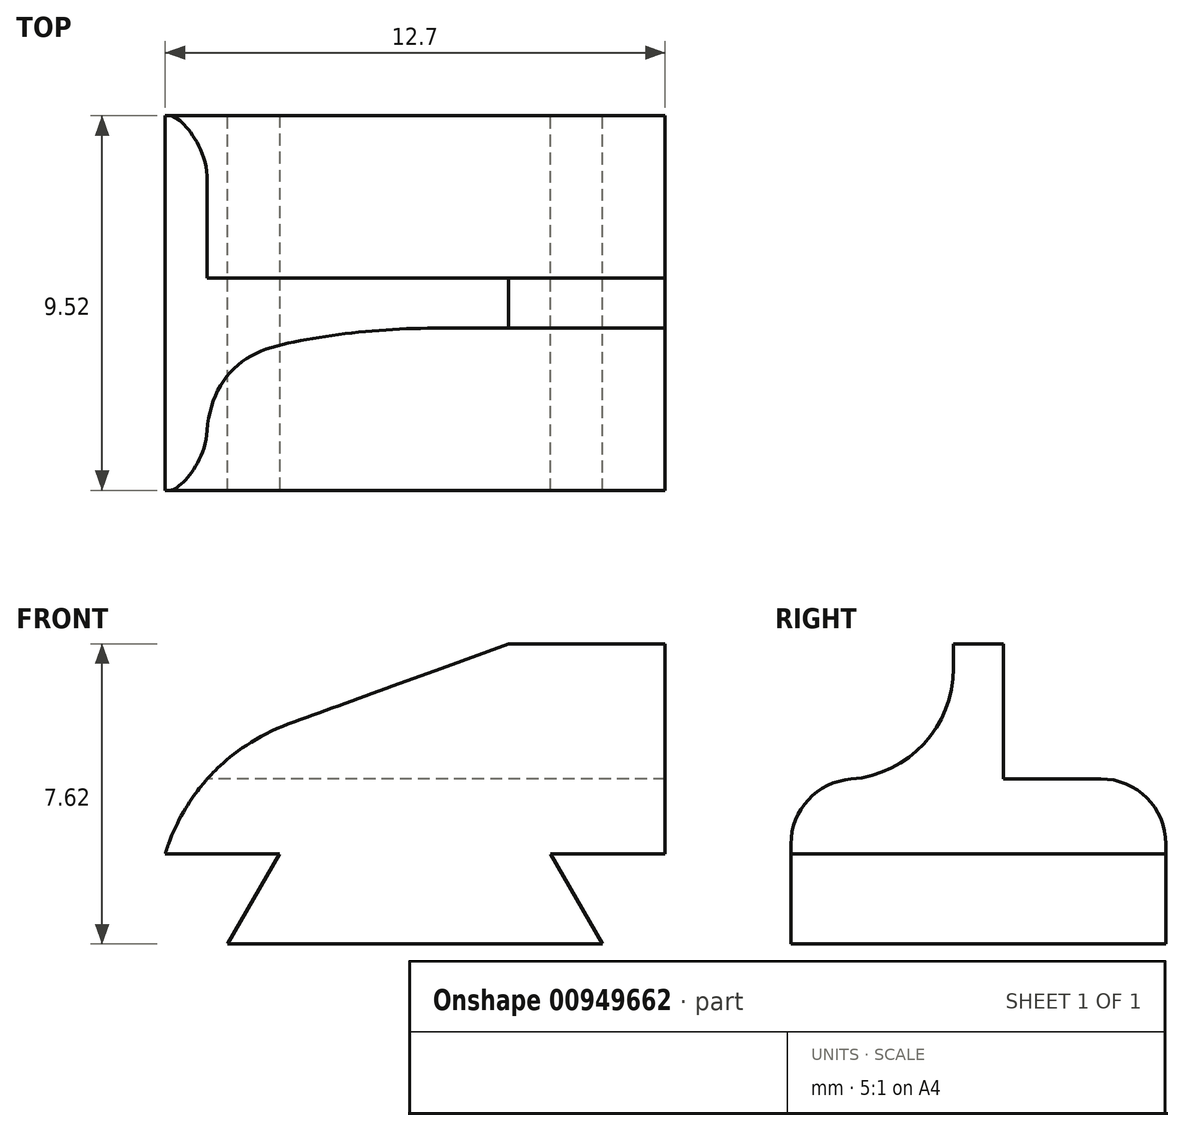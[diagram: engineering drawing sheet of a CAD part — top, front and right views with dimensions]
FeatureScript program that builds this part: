
annotation { "Feature Type Name" : "Feature", "Feature Type Description" : "" }
export const myFeature = defineFeature(function(context is Context, id is Id, definition is map)
    precondition{}
    {
        {
            var Q0;
            Q0=qCreatedBy(makeId("Top.planeOp"),FACE);
            var sketch = newSketch(context, id + "F0", { "sketchPlane" : qUnion([Q0])});
            skLineSegment(sketch, "E0.bottom", {"start": v(4.76, 4.76) * mm, "end": v(-4.76, 4.76) * mm});
            skLineSegment(sketch, "E0.top", {"start": v(4.76, -4.76) * mm, "end": v(-4.76, -4.76) * mm});
            skLineSegment(sketch, "E0.left", {"start": v(4.76, 4.76) * mm, "end": v(4.76, -4.76) * mm});
            skLineSegment(sketch, "E0.right", {"start": v(-4.76, 4.76) * mm, "end": v(-4.76, -4.76) * mm});
            skPoint(sketch, "E0.middle", {"position": v(0, 0) * mm});
            skSolve(sketch);
        }
        {
            var Q0;
            Q0=makeQuery(id+"F0.imprint","IMPRINT",FACE,{"disambiguationData":[TD([[makeQuery(id+"F0.imprint","IMPRINT",EDGE,{"derivedFrom":sQuery(id+"F0.wireOp",EDGE,"E0.bottom")}),1.0]])]});
            extrude(context, id + "F1", {"entities" : qUnion([Q0]), "depth" : 2.3 * mm, "offsetDistance" : 25.4 * mm});
        }
        {
            var Q0;
            Q0=makeQuery(id+"F1.opExtrude","CAP_EDGE",EDGE,{"disambiguationData":[OSD([sQuery(id+"F0.wireOp",EDGE,"E0.right")])],"isStart":false});
            var Q1;
            Q1=makeQuery(id+"F1.opExtrude","CAP_EDGE",EDGE,{"disambiguationData":[OSD([sQuery(id+"F0.wireOp",EDGE,"E0.left")])],"isStart":false});
            chamfer(context, id + "F2", {"entities" : qUnion([Q0, Q1]), "chamferType" : ChamferType.OFFSET_ANGLE, "width" : 1.32 * mm, "oppositeDirection" : false, "angle" : 60 * degree, "tangentPropagation" : true});
        }
        {
            var Q0;
            Q0=makeQuery(id+"F1.opExtrude","CAP_FACE",FACE,{"disambiguationData":[OSD([sQuery(id+"F0.wireOp",EDGE,"E0.bottom"),sQuery(id+"F0.wireOp",EDGE,"E0.top"),sQuery(id+"F0.wireOp",EDGE,"E0.left"),sQuery(id+"F0.wireOp",EDGE,"E0.right")])],"isStart":false});
            var sketch = newSketch(context, id + "F3", { "sketchPlane" : qUnion([Q0])});
            skLineSegment(sketch, "E1.bottom", {"start": v(6.35, -4.76) * mm, "end": v(-6.35, -4.76) * mm});
            skLineSegment(sketch, "E1.top", {"start": v(6.35, 4.76) * mm, "end": v(-6.35, 4.76) * mm});
            skLineSegment(sketch, "E1.left", {"start": v(6.35, -4.76) * mm, "end": v(6.35, 4.76) * mm});
            skLineSegment(sketch, "E1.right", {"start": v(-6.35, -4.76) * mm, "end": v(-6.35, 4.76) * mm});
            skPoint(sketch, "E1.middle", {"position": v(0, 0) * mm});
            skSolve(sketch);
        }
        {
            var Q0;
            {var subQ0=sQuery(id+"F3.wireOp",EDGE,"E1.left");Q0=makeQuery(id+"F3.imprint","IMPRINT",FACE,{"disambiguationData":[TD([[makeQuery(id+"F3.imprint","IMPRINT",EDGE,{"derivedFrom":subQ0}),1.0]])]});}
            var Q1;
            {var subQ0=sQuery(id+"F3.wireOp",EDGE,"E1.bottom");var subQ1=sQuery(id+"F0.wireOp",EDGE,"E0.right");var subQ2=sQuery(id+"F0.wireOp",EDGE,"E0.left");var subQ3=makeQuery(id+"F1.opExtrude","CAP_FACE",FACE,{"disambiguationData":[OSD([sQuery(id+"F0.wireOp",EDGE,"E0.bottom"),sQuery(id+"F0.wireOp",EDGE,"E0.top"),subQ2,subQ1])],"isStart":false});var subQ4=makeQuery(id+"F2.opChamfer","BLEND_EDGE",EDGE,{"blendedFrom":[makeQuery(id+"F1.opExtrude","CAP_EDGE",EDGE,{"disambiguationData":[OSD([subQ2])],"isStart":false}),subQ3],"blendedInto":[subQ3]});var subQ5=makeQuery(id+"F3.imprint","INTERSECT",VERTEX,{"derivedFrom":[subQ4,subQ0]});Q1=makeQuery(id+"F3.imprint","IMPRINT",FACE,{"disambiguationData":[TD([[makeQuery(id+"F3.imprint","IMPRINT",EDGE,{"disambiguationData":[TD([[subQ5,-1.0]])],"derivedFrom":subQ0}),-1.0]])]});}
            var Q2;
            {var subQ0=sQuery(id+"F3.wireOp",EDGE,"E1.right");Q2=makeQuery(id+"F3.imprint","IMPRINT",FACE,{"disambiguationData":[TD([[makeQuery(id+"F3.imprint","IMPRINT",EDGE,{"derivedFrom":subQ0}),-1.0]])]});}
            extrude(context, id + "F4", {"entities" : qUnion([Q0, Q1, Q2]), "operationType" : NewBodyOperationType.ADD, "depth" : 1.9 * mm, "offsetDistance" : 25.4 * mm});
        }
        {
            var Q0;
            Q0=makeQuery(id+"F4.opExtrude","CAP_EDGE",EDGE,{"disambiguationData":[OSD([sQuery(id+"F3.wireOp",EDGE,"E1.top")])],"isStart":false});
            var Q1;
            Q1=makeQuery(id+"F4.opExtrude","CAP_EDGE",EDGE,{"disambiguationData":[OSD([sQuery(id+"F3.wireOp",EDGE,"E1.bottom")])],"isStart":false});
            fillet(context, id + "F5", {"entities" : qUnion([Q0, Q1]), "radius" : 1.66 * mm, "tangentPropagation" : true, "allowEdgeOverflow" : false});
        }
        {
            var Q0;
            Q0=makeQuery(id+"F4.opExtrude","CAP_FACE",FACE,{"disambiguationData":[OSD([sQuery(id+"F3.wireOp",EDGE,"E1.bottom"),sQuery(id+"F3.wireOp",EDGE,"E1.top"),sQuery(id+"F3.wireOp",EDGE,"E1.left"),sQuery(id+"F3.wireOp",EDGE,"E1.right")])],"isStart":false});
            var sketch = newSketch(context, id + "F6", { "sketchPlane" : qUnion([Q0])});
            skLineSegment(sketch, "E2.bottom", {"start": v(6.35, -0.63) * mm, "end": v(-6.35, -0.64) * mm});
            skLineSegment(sketch, "E2.top", {"start": v(6.35, 0.64) * mm, "end": v(-6.35, 0.63) * mm});
            skLineSegment(sketch, "E2.left", {"start": v(6.35, -0.63) * mm, "end": v(6.35, 0.64) * mm});
            skLineSegment(sketch, "E2.right", {"start": v(-6.35, -0.64) * mm, "end": v(-6.35, 0.63) * mm});
            skPoint(sketch, "E2.middle", {"position": v(0, 0) * mm});
            skSolve(sketch);
        }
        {
            var Q0;
            Q0=makeQuery(id+"F6.imprint","IMPRINT",FACE,{"disambiguationData":[TD([[makeQuery(id+"F6.imprint","IMPRINT",EDGE,{"derivedFrom":sQuery(id+"F6.wireOp",EDGE,"E2.bottom")}),-1.0]])]});
            extrude(context, id + "F7", {"entities" : qUnion([Q0]), "operationType" : NewBodyOperationType.ADD, "depth" : 3.43 * mm, "offsetDistance" : 25.4 * mm});
        }
        {
            var Q0;
            Q0=makeQuery(id+"F7.opExtrude","CAP_EDGE",EDGE,{"disambiguationData":[OSD([sQuery(id+"F6.wireOp",EDGE,"E2.right")])],"isStart":false});
            chamfer(context, id + "F8", {"entities" : qUnion([Q0]), "chamferType" : ChamferType.OFFSET_ANGLE, "width" : 3.17 * mm, "oppositeDirection" : false, "angle" : 70 * degree, "tangentPropagation" : true});
        }
        {
            var Q0;
            Q0=makeQuery(id+"F7.opExtrude","CAP_EDGE",EDGE,{"disambiguationData":[OSD([sQuery(id+"F6.wireOp",EDGE,"E2.bottom")])],"isStart":true});
            var Q1;
            Q1=makeQuery(id+"F7.opExtrude","CAP_EDGE",EDGE,{"disambiguationData":[OSD([sQuery(id+"F6.wireOp",EDGE,"E2.top")])],"isStart":true});
            fillet(context, id + "F9", {"entities" : qUnion([Q0, Q1]), "radius" : 2.82 * mm, "tangentPropagation" : true, "allowEdgeOverflow" : false});
        }
        {
            var Q0;
            {var subQ0=sQuery(id+"F6.wireOp",EDGE,"E2.right");Q0=makeQuery(id+"F8.opChamfer","BLEND_EDGE",EDGE,{"blendedFrom":[makeQuery(id+"F7.opExtrude","CAP_EDGE",EDGE,{"disambiguationData":[OSD([subQ0])],"isStart":false}),makeQuery(id+"F7.boolean.opBoolean","MERGE",FACE,{"derivedFrom":[makeQuery(id+"F4.opExtrude","SWEPT_FACE",FACE,{"disambiguationData":[OSD([sQuery(id+"F3.wireOp",EDGE,"E1.right")])]}),makeQuery(id+"F7.opExtrude","SWEPT_FACE",FACE,{"disambiguationData":[OSD([subQ0])]})]})],"blendedInto":[makeQuery(id+"F7.boolean.opBoolean","MERGE",FACE,{"derivedFrom":[makeQuery(id+"F4.opExtrude","SWEPT_FACE",FACE,{"disambiguationData":[OSD([sQuery(id+"F3.wireOp",EDGE,"E1.right")])]}),makeQuery(id+"F7.opExtrude","SWEPT_FACE",FACE,{"disambiguationData":[OSD([subQ0])]})]})]});}
            fillet(context, id + "F10", {"entities" : qUnion([Q0]), "radius" : 5.08 * mm, "tangentPropagation" : true, "allowEdgeOverflow" : false});
        }
    });
